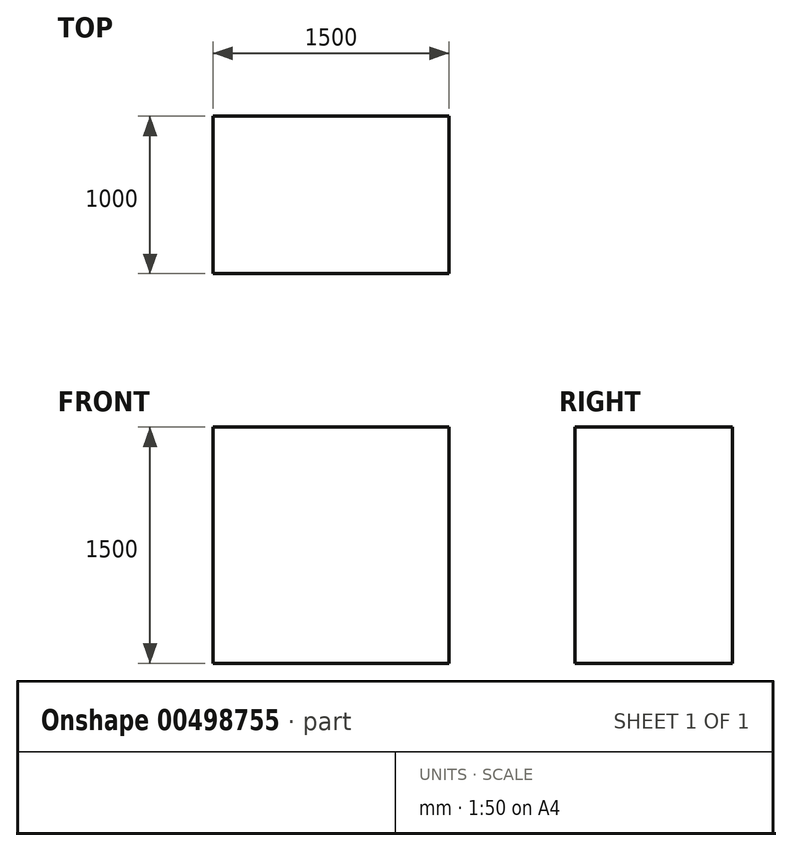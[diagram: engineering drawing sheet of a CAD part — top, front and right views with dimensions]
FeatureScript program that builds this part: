
annotation { "Feature Type Name" : "Feature", "Feature Type Description" : "" }
export const myFeature = defineFeature(function(context is Context, id is Id, definition is map)
    precondition{}
    {
        {
            var Q0;
            Q0=qCreatedBy(makeId("Front.planeOp"),FACE);
            var sketch = newSketch(context, id + "F0", { "sketchPlane" : qUnion([Q0])});
            skLineSegment(sketch, "E0.bottom", {"start": v(-1296.74, 744.96) * mm, "end": v(203.26, 744.96) * mm});
            skLineSegment(sketch, "E0.top", {"start": v(-1296.74, -755.04) * mm, "end": v(203.26, -755.04) * mm});
            skLineSegment(sketch, "E0.left", {"start": v(-1296.74, 744.96) * mm, "end": v(-1296.74, -755.04) * mm});
            skLineSegment(sketch, "E0.right", {"start": v(203.26, 744.96) * mm, "end": v(203.26, -755.04) * mm});
            skSolve(sketch);
        }
        {
            var Q0;
            Q0 = qSketchRegion(id + "F0", true);
            extrude(context, id + "F1", {"entities" : qUnion([Q0]), "endBound" : BoundingType.SYMMETRIC, "depth" : 1000 * mm});
        }
    });
